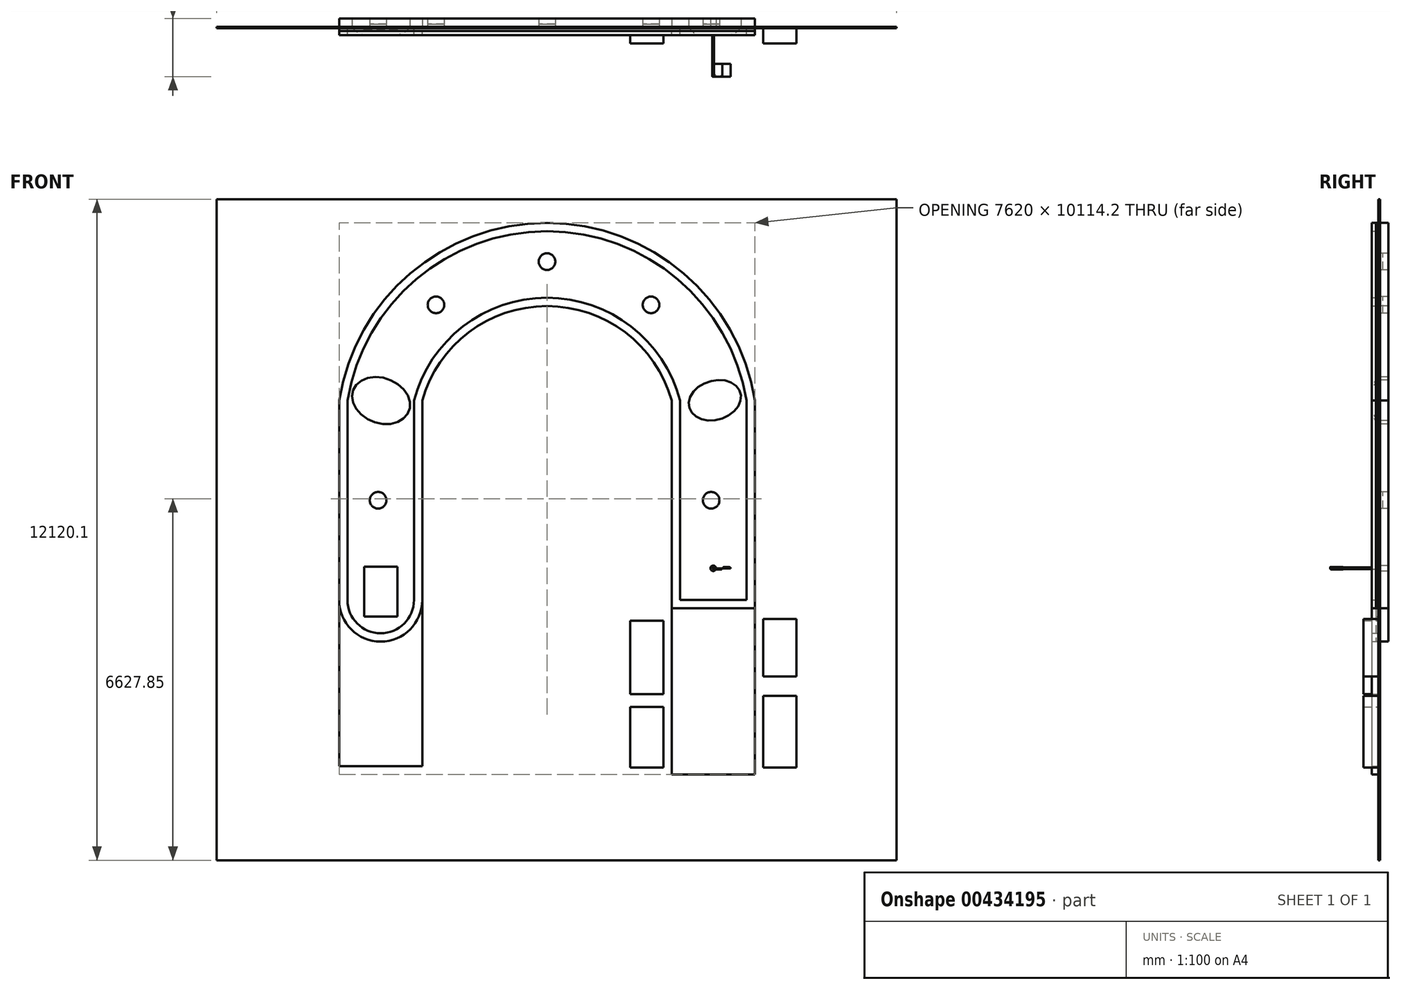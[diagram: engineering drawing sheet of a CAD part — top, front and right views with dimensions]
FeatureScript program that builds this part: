
annotation { "Feature Type Name" : "Feature", "Feature Type Description" : "" }
export const myFeature = defineFeature(function(context is Context, id is Id, definition is map)
    precondition{}
    {
        {
            var Q0;
            Q0=qCreatedBy(makeId("Front.planeOp"),FACE);
            var sketch = newSketch(context, id + "F0", { "sketchPlane" : qUnion([Q0])});
            skArc(sketch, "E0", {"start": v(816.67, 0) * mm, "mid": v(-1621.73, 1884.6) * mm, "end": v(-4060.13, 0) * mm});
            skLineSegment(sketch, "E1", {"start": v(-4060.13, 0) * mm, "end": v(-4060.13, -3657.6) * mm});
            skLineSegment(sketch, "E2", {"start": v(816.67, 0) * mm, "end": v(816.67, -3657.6) * mm});
            skPoint(sketch, "E3", {"position": v(-5279.33, -3657.6) * mm});
            skPoint(sketch, "E4", {"position": v(2035.87, -3657.6) * mm});
            skLineSegment(sketch, "E5", {"start": v(-5279.33, -3657.6) * mm, "end": v(-5279.33, 0) * mm});
            skLineSegment(sketch, "E6", {"start": v(2035.87, -3657.6) * mm, "end": v(2035.87, 0) * mm});
            skArc(sketch, "E7", {"start": v(2035.87, 0) * mm, "mid": v(-1621.73, 3103.8) * mm, "end": v(-5279.33, 0) * mm});
            skPoint(sketch, "E8", {"position": v(-1621.73, 3103.8) * mm});
            skPoint(sketch, "E9", {"position": v(-1621.73, 1884.6) * mm});
            skArc(sketch, "E10", {"start": v(-5279.33, -3657.6) * mm, "mid": v(-4669.73, -4267.2) * mm, "end": v(-4060.13, -3657.6) * mm});
            skPoint(sketch, "E11", {"position": v(-5431.73, 0) * mm});
            skPoint(sketch, "E12", {"position": v(-5431.73, -3657.6) * mm});
            skLineSegment(sketch, "E13", {"start": v(-5431.73, 0) * mm, "end": v(-5431.73, -3767.79) * mm});
            skPoint(sketch, "E14", {"position": v(2188.27, 0.2) * mm});
            skPoint(sketch, "E15", {"position": v(2188.27, -3657.6) * mm});
            skLineSegment(sketch, "E16", {"start": v(2188.27, 0.2) * mm, "end": v(2188.27, -3657.6) * mm});
            skArc(sketch, "E17", {"start": v(2188.27, 0.2) * mm, "mid": v(-1621.82, 3256.2) * mm, "end": v(-5431.73, 0) * mm});
            skPoint(sketch, "E18", {"position": v(-1621.73, 3256.2) * mm});
            skLineSegment(sketch, "E19", {"start": v(-3907.73, 0) * mm, "end": v(-3907.73, -3657.6) * mm});
            skLineSegment(sketch, "E20", {"start": v(664.27, -3657.6) * mm, "end": v(664.27, 0) * mm});
            skArc(sketch, "E21", {"start": v(-5431.73, -3657.6) * mm, "mid": v(-4669.73, -4419.6) * mm, "end": v(-3907.73, -3657.6) * mm});
            skPoint(sketch, "E22", {"position": v(-4669.73, -4267.2) * mm});
            skPoint(sketch, "E23", {"position": v(-4669.73, -4419.6) * mm});
            skArc(sketch, "E24", {"start": v(664.27, 0) * mm, "mid": v(-1621.73, 1732.2) * mm, "end": v(-3907.73, 0) * mm});
            skPoint(sketch, "E25", {"position": v(-1621.73, 1732.2) * mm});
            skLineSegment(sketch, "E26", {"start": v(664.27, -3657.6) * mm, "end": v(2188.27, -3657.6) * mm});
            skPoint(sketch, "E27", {"position": v(816.67, -3657.6) * mm});
            skLineSegment(sketch, "E28.0", {"start": v(664.27, -3810) * mm, "end": v(2188.27, -3810) * mm});
            skLineSegment(sketch, "E29", {"start": v(664.27, -3810) * mm, "end": v(664.27, -3657.6) * mm});
            skLineSegment(sketch, "E30", {"start": v(2188.27, -3657.6) * mm, "end": v(2188.27, -3810) * mm});
            skPoint(sketch, "E31", {"position": v(1426.27, -3075.78) * mm});
            skCircle(sketch, "E32", {"center": v(1426.27, -3075.78) * mm, "radius": 50.8 * mm});
            skLineSegment(sketch, "E33.bottom", {"start": v(-4974.53, -3048) * mm, "end": v(-4364.93, -3048) * mm});
            skLineSegment(sketch, "E33.top", {"start": v(-4974.53, -3962.4) * mm, "end": v(-4364.93, -3962.4) * mm});
            skLineSegment(sketch, "E33.left", {"start": v(-4974.53, -3048) * mm, "end": v(-4974.53, -3962.4) * mm});
            skLineSegment(sketch, "E33.right", {"start": v(-4364.93, -3048) * mm, "end": v(-4364.93, -3962.4) * mm});
            skEllipse(sketch, "E34", {"center": v(-4663.41, 0) * mm, "majorRadius": 547.1 * mm, "minorRadius": 413.28 * mm, "majorAxis": v(-0.94, 0.35)});
            skLineSegment(sketch, "E35", {"start": v(-3907.73, -3657.6) * mm, "end": v(-3907.73, -6705.6) * mm});
            skLineSegment(sketch, "E36", {"start": v(-3907.73, -6705.6) * mm, "end": v(-5431.73, -6705.6) * mm});
            skLineSegment(sketch, "E37", {"start": v(-5431.73, -3657.6) * mm, "end": v(-5431.73, -6705.6) * mm});
            skLineSegment(sketch, "E38", {"start": v(2188.27, -3810) * mm, "end": v(2188.27, -6858) * mm});
            skLineSegment(sketch, "E39", {"start": v(2188.27, -6858) * mm, "end": v(664.27, -6858) * mm});
            skLineSegment(sketch, "E40", {"start": v(664.27, -3810) * mm, "end": v(664.27, -6858) * mm});
            skCircle(sketch, "E41", {"center": v(-4716.79, -1828.8) * mm, "radius": 152.4 * mm});
            skPoint(sketch, "E41.centerSnap0", {"position": v(-4060.13, -1828.8) * mm});
            skCircle(sketch, "E42", {"center": v(-3655.57, 1754.36) * mm, "radius": 152.4 * mm});
            skCircle(sketch, "E43", {"center": v(-1621.73, 2547.6) * mm, "radius": 152.4 * mm});
            skCircle(sketch, "E44", {"center": v(285.76, 1754.36) * mm, "radius": 152.4 * mm});
            skCircle(sketch, "E45", {"center": v(1387.91, -1828.8) * mm, "radius": 152.4 * mm});
            skPoint(sketch, "E46", {"position": v(-3600.66, 1896.53) * mm});
            skPoint(sketch, "E47", {"position": v(-1621.73, 2700) * mm});
            skPoint(sketch, "E48", {"position": v(285.76, 1906.76) * mm});
            skPoint(sketch, "E49", {"position": v(1470.76, -1700.89) * mm});
            skPoint(sketch, "E50", {"position": v(-4731.52, -1677.11) * mm});
            skPoint(sketch, "E51", {"position": v(-5109.33, 298.79) * mm});
            skPoint(sketch, "E52", {"position": v(-4151.57, -193.25) * mm});
            skPoint(sketch, "E53", {"position": v(2025.48, 185.61) * mm});
            skEllipse(sketch, "E54", {"center": v(1456.96, 5.78) * mm, "majorRadius": 486.46 * mm, "minorRadius": 360.05 * mm, "majorAxis": v(-0.96, -0.28)});
            skLineSegment(sketch, "E55.bottom", {"start": v(-7678.37, 3691.36) * mm, "end": v(4789.68, 3691.36) * mm});
            skLineSegment(sketch, "E55.top", {"start": v(-7678.37, -8428.75) * mm, "end": v(4789.68, -8428.75) * mm});
            skLineSegment(sketch, "E55.left", {"start": v(-7678.37, 3691.36) * mm, "end": v(-7678.37, -8428.75) * mm});
            skLineSegment(sketch, "E55.right", {"start": v(4789.68, 3691.36) * mm, "end": v(4789.68, -8428.75) * mm});
            skLineSegment(sketch, "E56.bottom", {"start": v(2340.67, -4007.48) * mm, "end": v(2950.27, -4007.48) * mm});
            skLineSegment(sketch, "E56.top", {"start": v(2340.67, -5059.45) * mm, "end": v(2950.27, -5059.45) * mm});
            skLineSegment(sketch, "E56.left", {"start": v(2340.67, -4007.48) * mm, "end": v(2340.67, -5059.45) * mm});
            skLineSegment(sketch, "E56.right", {"start": v(2950.27, -4007.48) * mm, "end": v(2950.27, -5059.45) * mm});
            skLineSegment(sketch, "E57.bottom", {"start": v(2340.67, -5415.26) * mm, "end": v(2950.27, -5415.26) * mm});
            skLineSegment(sketch, "E57.top", {"start": v(2340.67, -6730.22) * mm, "end": v(2950.27, -6730.22) * mm});
            skLineSegment(sketch, "E57.left", {"start": v(2340.67, -5415.26) * mm, "end": v(2340.67, -6730.22) * mm});
            skLineSegment(sketch, "E57.right", {"start": v(2950.27, -5415.26) * mm, "end": v(2950.27, -6730.22) * mm});
            skLineSegment(sketch, "E58.bottom", {"start": v(-97.73, -4038.42) * mm, "end": v(511.87, -4038.42) * mm});
            skLineSegment(sketch, "E58.top", {"start": v(-97.73, -5384.32) * mm, "end": v(511.87, -5384.32) * mm});
            skLineSegment(sketch, "E58.left", {"start": v(-97.73, -4038.42) * mm, "end": v(-97.73, -5384.32) * mm});
            skLineSegment(sketch, "E58.right", {"start": v(511.87, -4038.42) * mm, "end": v(511.87, -5384.32) * mm});
            skLineSegment(sketch, "E59.bottom", {"start": v(-97.73, -5616.37) * mm, "end": v(511.87, -5616.37) * mm});
            skLineSegment(sketch, "E59.top", {"start": v(-97.73, -6730.22) * mm, "end": v(511.87, -6730.22) * mm});
            skLineSegment(sketch, "E59.left", {"start": v(-97.73, -5616.37) * mm, "end": v(-97.73, -6730.22) * mm});
            skLineSegment(sketch, "E59.right", {"start": v(511.87, -5616.37) * mm, "end": v(511.87, -6730.22) * mm});
            skCircle(sketch, "E60", {"center": v(1426.27, -3075.78) * mm, "radius": 14.57 * mm});
            skSolve(sketch);
        }
        {
            var Q0;
            Q0=makeQuery(id+"F0.imprint","IMPRINT",FACE,{"disambiguationData":[TD([[makeQuery(id+"F0.imprint","IMPRINT",EDGE,{"derivedFrom":sQuery(id+"F0.wireOp",EDGE,"E28.0")}),1.0]])]});
            var Q1;
            Q1=makeQuery(id+"F0.imprint","IMPRINT",FACE,{"disambiguationData":[TD([[makeQuery(id+"F0.imprint","IMPRINT",EDGE,{"derivedFrom":sQuery(id+"F0.wireOp",EDGE,"E0")}),1.0]])]});
            var Q2;
            Q2=makeQuery(id+"F0.imprint","IMPRINT",FACE,{"disambiguationData":[TD([[makeQuery(id+"F0.imprint","IMPRINT",EDGE,{"derivedFrom":sQuery(id+"F0.wireOp",EDGE,"E0")}),-1.0]])]});
            var Q3;
            Q3=makeQuery(id+"F0.imprint","IMPRINT",FACE,{"disambiguationData":[TD([[makeQuery(id+"F0.imprint","IMPRINT",EDGE,{"derivedFrom":sQuery(id+"F0.wireOp",EDGE,"E33.bottom")}),-1.0]])]});
            var Q4;
            Q4=makeQuery(id+"F0.imprint","IMPRINT",FACE,{"disambiguationData":[TD([[makeQuery(id+"F0.imprint","IMPRINT",EDGE,{"derivedFrom":sQuery(id+"F0.wireOp",EDGE,"E32")}),1.0]])]});
            extrude(context, id + "F1", {"entities" : qUnion([Q0, Q1, Q2, Q3, Q4]), "oppositeDirection" : true, "depth" : 152.4 * mm});
        }
        {
            var Q0;
            Q0=makeQuery(id+"F0.imprint","IMPRINT",FACE,{"disambiguationData":[TD([[makeQuery(id+"F0.imprint","IMPRINT",EDGE,{"derivedFrom":sQuery(id+"F0.wireOp",EDGE,"E32")}),1.0]])]});
            extrude(context, id + "F2", {"entities" : qUnion([Q0]), "operationType" : NewBodyOperationType.REMOVE, "oppositeDirection" : true, "depth" : 152.4 * mm});
        }
        {
            var Q0;
            Q0=makeQuery(id+"F0.imprint","IMPRINT",FACE,{"disambiguationData":[TD([[makeQuery(id+"F0.imprint","IMPRINT",EDGE,{"derivedFrom":sQuery(id+"F0.wireOp",EDGE,"E0")}),1.0]])]});
            var Q1;
            Q1=makeQuery(id+"F0.imprint","IMPRINT",FACE,{"disambiguationData":[TD([[makeQuery(id+"F0.imprint","IMPRINT",EDGE,{"derivedFrom":sQuery(id+"F0.wireOp",EDGE,"E28.0")}),1.0]])]});
            extrude(context, id + "F3", {"entities" : qUnion([Q0, Q1]), "depth" : 76.2 * mm});
        }
        {
            var Q0;
            Q0=makeQuery(id+"F0.imprint","IMPRINT",FACE,{"disambiguationData":[TD([[makeQuery(id+"F0.imprint","IMPRINT",EDGE,{"derivedFrom":sQuery(id+"F0.wireOp",EDGE,"E0")}),-1.0]])]});
            extrude(context, id + "F4", {"entities" : qUnion([Q0]), "depth" : 25.4 * mm});
        }
        {
            var Q0;
            Q0=makeQuery(id+"F0.imprint","IMPRINT",FACE,{"disambiguationData":[TD([[makeQuery(id+"F0.imprint","IMPRINT",EDGE,{"derivedFrom":sQuery(id+"F0.wireOp",EDGE,"E33.bottom")}),-1.0]])]});
            extrude(context, id + "F5", {"entities" : qUnion([Q0]), "depth" : 38.1 * mm});
        }
        {
            var Q0;
            Q0=makeQuery(id+"F0.imprint","IMPRINT",FACE,{"disambiguationData":[TD([[makeQuery(id+"F0.imprint","IMPRINT",EDGE,{"derivedFrom":sQuery(id+"F0.wireOp",EDGE,"E34")}),1.0]])]});
            extrude(context, id + "F6", {"entities" : qUnion([Q0]), "depth" : 152.4 * mm});
        }
        {
            var Q0;
            Q0=makeQuery(id+"F6.opExtrude","CAP_EDGE",EDGE,{"disambiguationData":[OSD([sQuery(id+"F0.wireOp",EDGE,"E34")])],"isStart":false});
            fillet(context, id + "F7", {"entities" : qUnion([Q0]), "radius" : 304.8 * mm, "tangentPropagation" : true, "allowEdgeOverflow" : false});
        }
        {
            var Q0;
            {var subQ0=sQuery(id+"F0.wireOp",EDGE,"E21");Q0=makeQuery(id+"F0.imprint","IMPRINT",FACE,{"disambiguationData":[TD([[makeQuery(id+"F0.imprint","IMPRINT",EDGE,{"derivedFrom":subQ0}),-1.0]])]});}
            extrude(context, id + "F8", {"entities" : qUnion([Q0]), "depth" : 152.4 * mm});
        }
        {
            var Q0;
            Q0=makeQuery(id+"F0.imprint","IMPRINT",FACE,{"disambiguationData":[TD([[makeQuery(id+"F0.imprint","IMPRINT",EDGE,{"derivedFrom":sQuery(id+"F0.wireOp",EDGE,"E28.0")}),-1.0]])]});
            extrude(context, id + "F9", {"entities" : qUnion([Q0]), "depth" : 152.4 * mm});
        }
        {
            var Q0;
            {var subQ0=sQuery(id+"F0.wireOp",EDGE,"LoleBhoI-OBvs-xKIg-6yBj-jzxmYLrDXjGT");var subQ1=sQuery(id+"F0.wireOp",EDGE,"E7");var subQ2=makeQuery(id+"F0.imprint","INTERSECT",VERTEX,{"disambiguationData":[OD(0.0)],"derivedFrom":[subQ1,subQ0]});Q0=makeQuery(id+"F0.imprint","IMPRINT",FACE,{"disambiguationData":[TD([[makeQuery(id+"F0.imprint","IMPRINT",EDGE,{"disambiguationData":[TD([[subQ2,-1.0]])],"derivedFrom":subQ1}),1.0]])]});}
            extrude(context, id + "F10", {"entities" : qUnion([Q0]), "operationType" : NewBodyOperationType.ADD, "depth" : 30.48 * mm});
        }
        {
            var Q0;
            Q0=makeQuery(id+"F0.imprint","IMPRINT",FACE,{"disambiguationData":[TD([[makeQuery(id+"F0.imprint","IMPRINT",EDGE,{"derivedFrom":sQuery(id+"F0.wireOp",EDGE,"E54")}),1.0]])]});
            extrude(context, id + "F11", {"entities" : qUnion([Q0]), "depth" : 152.4 * mm});
        }
        {
            var Q0;
            Q0=makeQuery(id+"F11.opExtrude","CAP_FACE",FACE,{"disambiguationData":[OSD([sQuery(id+"F0.wireOp",EDGE,"E54")])],"isStart":false});
            fillet(context, id + "F12", {"entities" : qUnion([Q0]), "radius" : 265.18 * mm, "tangentPropagation" : true, "allowEdgeOverflow" : false});
        }
        {
            var Q0;
            Q0=makeQuery(id+"F0.imprint","IMPRINT",FACE,{"disambiguationData":[TD([[makeQuery(id+"F0.imprint","IMPRINT",EDGE,{"derivedFrom":sQuery(id+"F0.wireOp",EDGE,"E41")}),1.0]])]});
            extrude(context, id + "F13", {"entities" : qUnion([Q0]), "oppositeDirection" : true, "depth" : 50.8 * mm});
        }
        {
            var Q0;
            Q0=makeQuery(id+"F0.imprint","IMPRINT",FACE,{"disambiguationData":[TD([[makeQuery(id+"F0.imprint","IMPRINT",EDGE,{"derivedFrom":sQuery(id+"F0.wireOp",EDGE,"E45")}),1.0]])]});
            extrude(context, id + "F14", {"entities" : qUnion([Q0]), "oppositeDirection" : true, "depth" : 50.8 * mm});
        }
        {
            var Q0;
            Q0=makeQuery(id+"F0.imprint","IMPRINT",FACE,{"disambiguationData":[TD([[makeQuery(id+"F0.imprint","IMPRINT",EDGE,{"derivedFrom":sQuery(id+"F0.wireOp",EDGE,"E43")}),1.0]])]});
            extrude(context, id + "F15", {"entities" : qUnion([Q0]), "oppositeDirection" : true, "depth" : 50.8 * mm});
        }
        {
            var Q0;
            Q0=makeQuery(id+"F0.imprint","IMPRINT",FACE,{"disambiguationData":[TD([[makeQuery(id+"F0.imprint","IMPRINT",EDGE,{"derivedFrom":sQuery(id+"F0.wireOp",EDGE,"E42")}),1.0]])]});
            extrude(context, id + "F16", {"entities" : qUnion([Q0]), "oppositeDirection" : true, "depth" : 50.8 * mm});
        }
        {
            var Q0;
            Q0=makeQuery(id+"F0.imprint","IMPRINT",FACE,{"disambiguationData":[TD([[makeQuery(id+"F0.imprint","IMPRINT",EDGE,{"derivedFrom":sQuery(id+"F0.wireOp",EDGE,"E44")}),1.0]])]});
            extrude(context, id + "F17", {"entities" : qUnion([Q0]), "oppositeDirection" : true, "depth" : 50.8 * mm});
        }
        {
            var Q0;
            Q0 = qSketchRegion(id + "F0", true);
            extrude(context, id + "F18", {"entities" : qUnion([Q0]), "depth" : 30.48 * mm});
        }
        {
            var Q0;
            Q0=makeQuery(id+"F0.imprint","IMPRINT",FACE,{"disambiguationData":[TD([[makeQuery(id+"F0.imprint","IMPRINT",EDGE,{"derivedFrom":sQuery(id+"F0.wireOp",EDGE,"E58.bottom")}),-1.0]])]});
            extrude(context, id + "F19", {"entities" : qUnion([Q0]), "depth" : 304.8 * mm});
        }
        {
            var Q0;
            Q0=makeQuery(id+"F0.imprint","IMPRINT",FACE,{"disambiguationData":[TD([[makeQuery(id+"F0.imprint","IMPRINT",EDGE,{"derivedFrom":sQuery(id+"F0.wireOp",EDGE,"E56.bottom")}),-1.0]])]});
            extrude(context, id + "F20", {"entities" : qUnion([Q0]), "depth" : 304.8 * mm});
        }
        {
            var Q0;
            Q0=makeQuery(id+"F0.imprint","IMPRINT",FACE,{"disambiguationData":[TD([[makeQuery(id+"F0.imprint","IMPRINT",EDGE,{"derivedFrom":sQuery(id+"F0.wireOp",EDGE,"E59.bottom")}),-1.0]])]});
            extrude(context, id + "F21", {"entities" : qUnion([Q0]), "depth" : 304.8 * mm});
        }
        {
            var Q0;
            Q0=makeQuery(id+"F0.imprint","IMPRINT",FACE,{"disambiguationData":[TD([[makeQuery(id+"F0.imprint","IMPRINT",EDGE,{"derivedFrom":sQuery(id+"F0.wireOp",EDGE,"E57.bottom")}),-1.0]])]});
            extrude(context, id + "F22", {"entities" : qUnion([Q0]), "depth" : 304.8 * mm});
        }
        {
            var Q0;
            Q0=makeQuery(id+"F0.imprint","IMPRINT",FACE,{"disambiguationData":[TD([[makeQuery(id+"F0.imprint","IMPRINT",EDGE,{"derivedFrom":sQuery(id+"F0.wireOp",EDGE,"E0")}),-1.0]])]});
            extrude(context, id + "F23", {"entities" : qUnion([Q0]), "depth" : 30.48 * mm});
        }
        {
            var Q0;
            Q0=makeQuery(id+"F3.opExtrude","CAP_FACE",FACE,{"disambiguationData":[OSD([sQuery(id+"F0.wireOp",EDGE,"E0"),sQuery(id+"F0.wireOp",EDGE,"E1"),sQuery(id+"F0.wireOp",EDGE,"E2"),sQuery(id+"F0.wireOp",EDGE,"E5"),sQuery(id+"F0.wireOp",EDGE,"E6"),sQuery(id+"F0.wireOp",EDGE,"E7"),sQuery(id+"F0.wireOp",EDGE,"E10"),sQuery(id+"F0.wireOp",EDGE,"E13"),sQuery(id+"F0.wireOp",EDGE,"E16"),sQuery(id+"F0.wireOp",EDGE,"E17"),sQuery(id+"F0.wireOp",EDGE,"E19"),sQuery(id+"F0.wireOp",EDGE,"E20"),sQuery(id+"F0.wireOp",EDGE,"E21"),sQuery(id+"F0.wireOp",EDGE,"E24"),sQuery(id+"F0.wireOp",EDGE,"E26"),sQuery(id+"F0.wireOp",EDGE,"E28.0"),sQuery(id+"F0.wireOp",EDGE,"E29"),sQuery(id+"F0.wireOp",EDGE,"E30")])],"isStart":false});
            extrude(context, id + "F24", {"entities" : qUnion([Q0]), "depth" : 76.2 * mm});
        }
        {
            var Q0;
            Q0=makeQuery(id+"F5.opExtrude","CAP_FACE",FACE,{"disambiguationData":[OSD([sQuery(id+"F0.wireOp",EDGE,"E33.bottom"),sQuery(id+"F0.wireOp",EDGE,"E33.top"),sQuery(id+"F0.wireOp",EDGE,"E33.left"),sQuery(id+"F0.wireOp",EDGE,"E33.right")])],"isStart":false});
            extrude(context, id + "F25", {"entities" : qUnion([Q0]), "depth" : 38.1 * mm});
        }
        {
            var Q0;
            Q0=makeQuery(id+"F0.imprint","IMPRINT",FACE,{"disambiguationData":[TD([[makeQuery(id+"F0.imprint","IMPRINT",EDGE,{"derivedFrom":sQuery(id+"F0.wireOp",EDGE,"E60")}),1.0]])]});
            extrude(context, id + "F26", {"entities" : qUnion([Q0]), "depth" : 914.4 * mm});
        }
        {
            var Q0;
            Q0=makeQuery(id+"F26.opExtrude","CAP_EDGE",EDGE,{"disambiguationData":[OSD([sQuery(id+"F0.wireOp",EDGE,"E60")])],"isStart":false});
            cPlane(context, id + "F27", {"entities" : qUnion([Q0]), "cplaneType" : CPlaneType.LINE_ANGLE, "offset" : 25.4 * mm, "angle" : 360 * degree, "width" : 152.4 * mm, "height" : 152.4 * mm});
        }
        {
            var Q0;
            Q0=qCreatedBy(id+"F27.planeOp",FACE);
            var sketch = newSketch(context, id + "F28", { "sketchPlane" : qUnion([Q0])});
            skLineSegment(sketch, "E61", {"start": v(1440.4, 914.43) * mm, "end": v(1440.4, 680.77) * mm});
            skLineSegment(sketch, "E62", {"start": v(1440.4, 680.77) * mm, "end": v(1596.3, 680.77) * mm});
            skLineSegment(sketch, "E63", {"start": v(1596.3, 680.77) * mm, "end": v(1596.3, 914.43) * mm});
            skLineSegment(sketch, "E64", {"start": v(1596.3, 914.43) * mm, "end": v(1440.4, 914.43) * mm});
            skLineSegment(sketch, "E65", {"start": v(1596.3, 914.43) * mm, "end": v(1746.14, 914.43) * mm});
            skLineSegment(sketch, "E66", {"start": v(1746.14, 914.43) * mm, "end": v(1746.14, 680.77) * mm});
            skLineSegment(sketch, "E67", {"start": v(1746.14, 680.77) * mm, "end": v(1596.3, 680.77) * mm});
            skSolve(sketch);
        }
        {
            var Q0;
            Q0=makeQuery(id+"F28.imprint","IMPRINT",FACE,{"disambiguationData":[TD([[makeQuery(id+"F28.imprint","IMPRINT",EDGE,{"derivedFrom":sQuery(id+"F28.wireOp",EDGE,"E61")}),1.0]])]});
            extrude(context, id + "F29", {"entities" : qUnion([Q0]), "depth" : 22.86 * mm});
        }
        {
            var Q0;
            Q0=makeQuery(id+"F28.imprint","IMPRINT",FACE,{"disambiguationData":[TD([[makeQuery(id+"F28.imprint","IMPRINT",EDGE,{"derivedFrom":sQuery(id+"F28.wireOp",EDGE,"E63")}),-1.0]])]});
            extrude(context, id + "F30", {"entities" : qUnion([Q0]), "oppositeDirection" : true, "depth" : 22.86 * mm});
        }
        {
            var Q0;
            Q0=makeQuery(id+"F30.opExtrude","CAP_EDGE",EDGE,{"disambiguationData":[OSD([sQuery(id+"F28.wireOp",EDGE,"E63")])],"isStart":false});
            var Q1;
            Q1=makeQuery(id+"F29.opExtrude","CAP_EDGE",EDGE,{"disambiguationData":[OSD([sQuery(id+"F28.wireOp",EDGE,"E64")])],"isStart":false});
            var Q2;
            Q2=makeQuery(id+"F29.opExtrude","CAP_EDGE",EDGE,{"disambiguationData":[OSD([sQuery(id+"F28.wireOp",EDGE,"E61")])],"isStart":false});
            var Q3;
            Q3=makeQuery(id+"F30.opExtrude","CAP_EDGE",EDGE,{"disambiguationData":[OSD([sQuery(id+"F28.wireOp",EDGE,"E66")])],"isStart":false});
            var Q4;
            Q4=makeQuery(id+"F29.opExtrude","CAP_EDGE",EDGE,{"disambiguationData":[OSD([sQuery(id+"F28.wireOp",EDGE,"E63")])],"isStart":false});
            fillet(context, id + "F31", {"entities" : qUnion([Q0, Q1, Q2, Q3, Q4]), "radius" : 30.48 * mm, "tangentPropagation" : true, "allowEdgeOverflow" : false});
        }
    });
